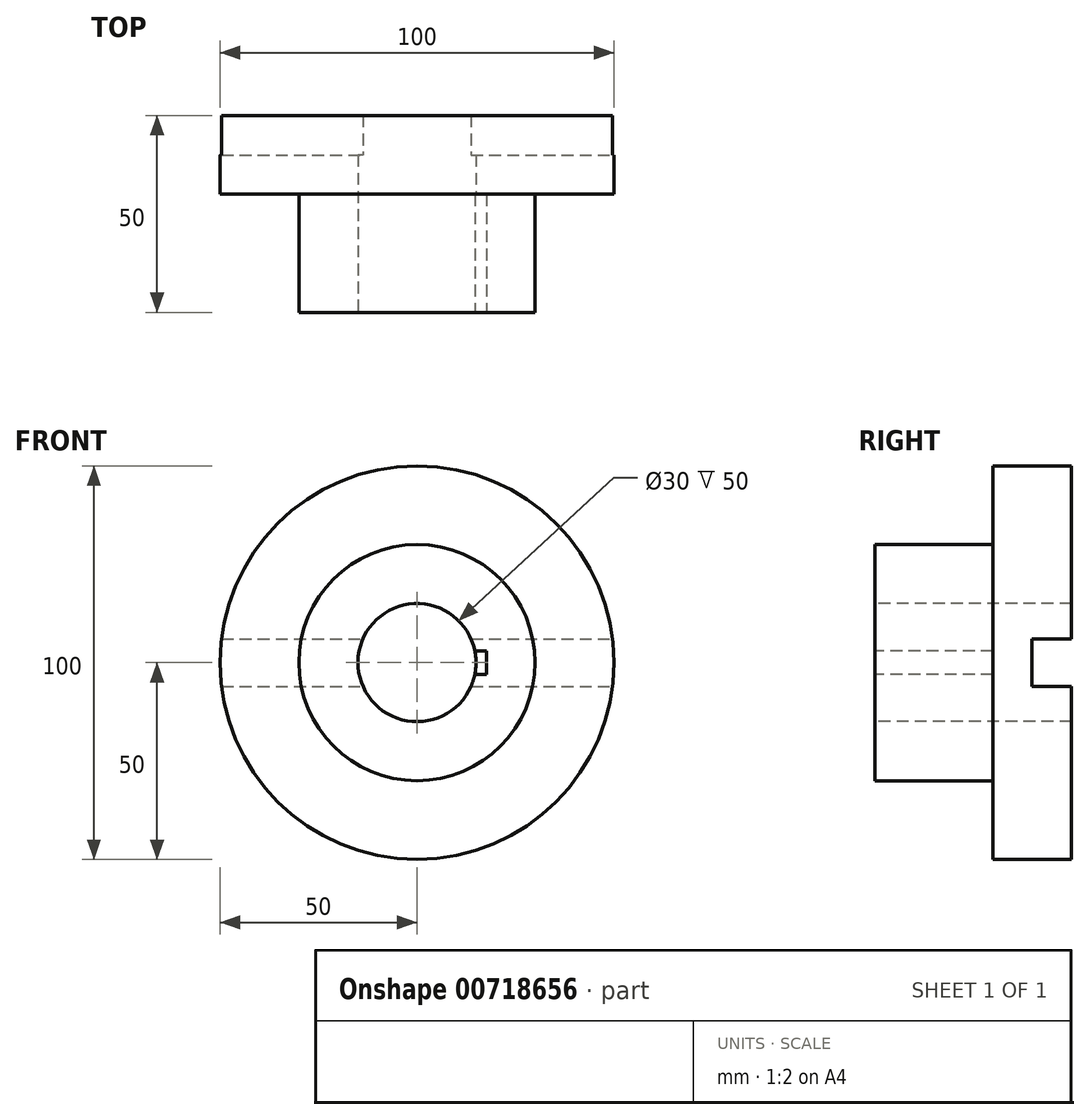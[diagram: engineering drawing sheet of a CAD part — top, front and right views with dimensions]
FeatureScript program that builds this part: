
annotation { "Feature Type Name" : "Feature", "Feature Type Description" : "" }
export const myFeature = defineFeature(function(context is Context, id is Id, definition is map)
    precondition{}
    {
        {
            var Q0;
            Q0=qCreatedBy(makeId("Top.planeOp"),FACE);
            var sketch = newSketch(context, id + "F0", { "sketchPlane" : qUnion([Q0])});
            skLineSegment(sketch, "E0", {"start": v(0, 0) * mm, "end": v(30, 0) * mm});
            skLineSegment(sketch, "E1", {"start": v(30, 0) * mm, "end": v(30, 30) * mm});
            skLineSegment(sketch, "E2", {"start": v(30, 30) * mm, "end": v(50, 30) * mm});
            skLineSegment(sketch, "E3", {"start": v(50, 30) * mm, "end": v(50, 50) * mm});
            skLineSegment(sketch, "E4", {"start": v(50, 50) * mm, "end": v(0, 50) * mm});
            skLineSegment(sketch, "E5", {"start": v(0, 50) * mm, "end": v(0, 0) * mm});
            skSolve(sketch);
        }
        {
            var Q0;
            Q0=makeQuery(id+"F0.imprint","IMPRINT",FACE,{"disambiguationData":[TD([[makeQuery(id+"F0.imprint","IMPRINT",EDGE,{"derivedFrom":sQuery(id+"F0.wireOp",EDGE,"E0")}),1.0]])]});
            var Q1;
            Q1=sQuery(id+"F0.wireOp",EDGE,"E5");
            revolve(context, id + "F1", {"surfaceOperationType" : NewSurfaceOperationType.NEW, "entities" : qUnion([Q0]), "axis" : qUnion([Q1]), "revolveType" : RevolveType.FULL});
        }
        {
            var Q0;
            Q0=makeQuery(id+"F1.opRevolve","SWEPT_FACE",FACE,{"disambiguationData":[OSD([sQuery(id+"F0.wireOp",EDGE,"E0")])]});
            var sketch = newSketch(context, id + "F2", { "sketchPlane" : qUnion([Q0])});
            skCircle(sketch, "E6", {"center": v(0, 0) * mm, "radius": 15 * mm});
            skLineSegment(sketch, "E7", {"start": v(-50.09, 0) * mm, "end": v(49.91, 0) * mm});
            skLineSegment(sketch, "E8", {"start": v(14.7, 3) * mm, "end": v(17.7, 3) * mm});
            skLineSegment(sketch, "E9", {"start": v(17.7, 3) * mm, "end": v(17.7, -3) * mm});
            skLineSegment(sketch, "E10", {"start": v(17.7, -3) * mm, "end": v(14.7, -3) * mm});
            skLineSegment(sketch, "E11", {"start": v(14.7, 3) * mm, "end": v(9.65, 3) * mm});
            skLineSegment(sketch, "E12", {"start": v(14.7, -3) * mm, "end": v(9.8, -3) * mm});
            skLineSegment(sketch, "E13", {"start": v(9.65, 3) * mm, "end": v(9.8, -3) * mm});
            skSolve(sketch);
        }
        {
            var Q0;
            {var subQ0=sQuery(id+"F2.wireOp",EDGE,"E11");Q0=makeQuery(id+"F2.imprint","IMPRINT",FACE,{"disambiguationData":[TD([[makeQuery(id+"F2.imprint","IMPRINT",EDGE,{"derivedFrom":subQ0}),1.0]])]});}
            var Q1;
            {var subQ0=sQuery(id+"F2.wireOp",EDGE,"E12");Q1=makeQuery(id+"F2.imprint","IMPRINT",FACE,{"disambiguationData":[TD([[makeQuery(id+"F2.imprint","IMPRINT",EDGE,{"derivedFrom":subQ0}),1.0]])]});}
            var Q2;
            {var subQ0=sQuery(id+"F2.wireOp",EDGE,"E12");Q2=makeQuery(id+"F2.imprint","IMPRINT",FACE,{"disambiguationData":[TD([[makeQuery(id+"F2.imprint","IMPRINT",EDGE,{"derivedFrom":subQ0}),-1.0]])]});}
            var Q3;
            {var subQ0=sQuery(id+"F2.wireOp",EDGE,"E11");Q3=makeQuery(id+"F2.imprint","IMPRINT",FACE,{"disambiguationData":[TD([[makeQuery(id+"F2.imprint","IMPRINT",EDGE,{"derivedFrom":subQ0}),-1.0]])]});}
            extrude(context, id + "F3", {"entities" : qUnion([Q0, Q1, Q2, Q3]), "operationType" : NewBodyOperationType.REMOVE, "endBound" : BoundingType.THROUGH_ALL, "oppositeDirection" : true, "depth" : 25 * mm, "offsetDistance" : 25 * mm});
        }
        {
            var Q0;
            Q0 = qSketchRegion(id + "F2", true);
            extrude(context, id + "F4", {"entities" : qUnion([Q0]), "operationType" : NewBodyOperationType.REMOVE, "oppositeDirection" : true, "depth" : 30 * mm, "offsetDistance" : 25 * mm});
        }
        {
            var Q0;
            Q0=makeQuery(id+"F1.opRevolve","SWEPT_FACE",FACE,{"disambiguationData":[OSD([sQuery(id+"F0.wireOp",EDGE,"E4")])]});
            var sketch = newSketch(context, id + "F5", { "sketchPlane" : qUnion([Q0])});
            skLineSegment(sketch, "E14.bottom", {"start": v(62.5, -6) * mm, "end": v(-62.5, -6) * mm});
            skLineSegment(sketch, "E14.top", {"start": v(62.5, 6) * mm, "end": v(-62.5, 6) * mm});
            skLineSegment(sketch, "E14.left", {"start": v(62.5, -6) * mm, "end": v(62.5, 6) * mm});
            skLineSegment(sketch, "E14.right", {"start": v(-62.5, -6) * mm, "end": v(-62.5, 6) * mm});
            skPoint(sketch, "E14.middle", {"position": v(0, 0) * mm});
            skSolve(sketch);
        }
        {
            var Q0;
            Q0 = qSketchRegion(id + "F5", true);
            extrude(context, id + "F6", {"entities" : qUnion([Q0]), "operationType" : NewBodyOperationType.REMOVE, "oppositeDirection" : true, "depth" : 10 * mm, "offsetDistance" : 25 * mm});
        }
    });
